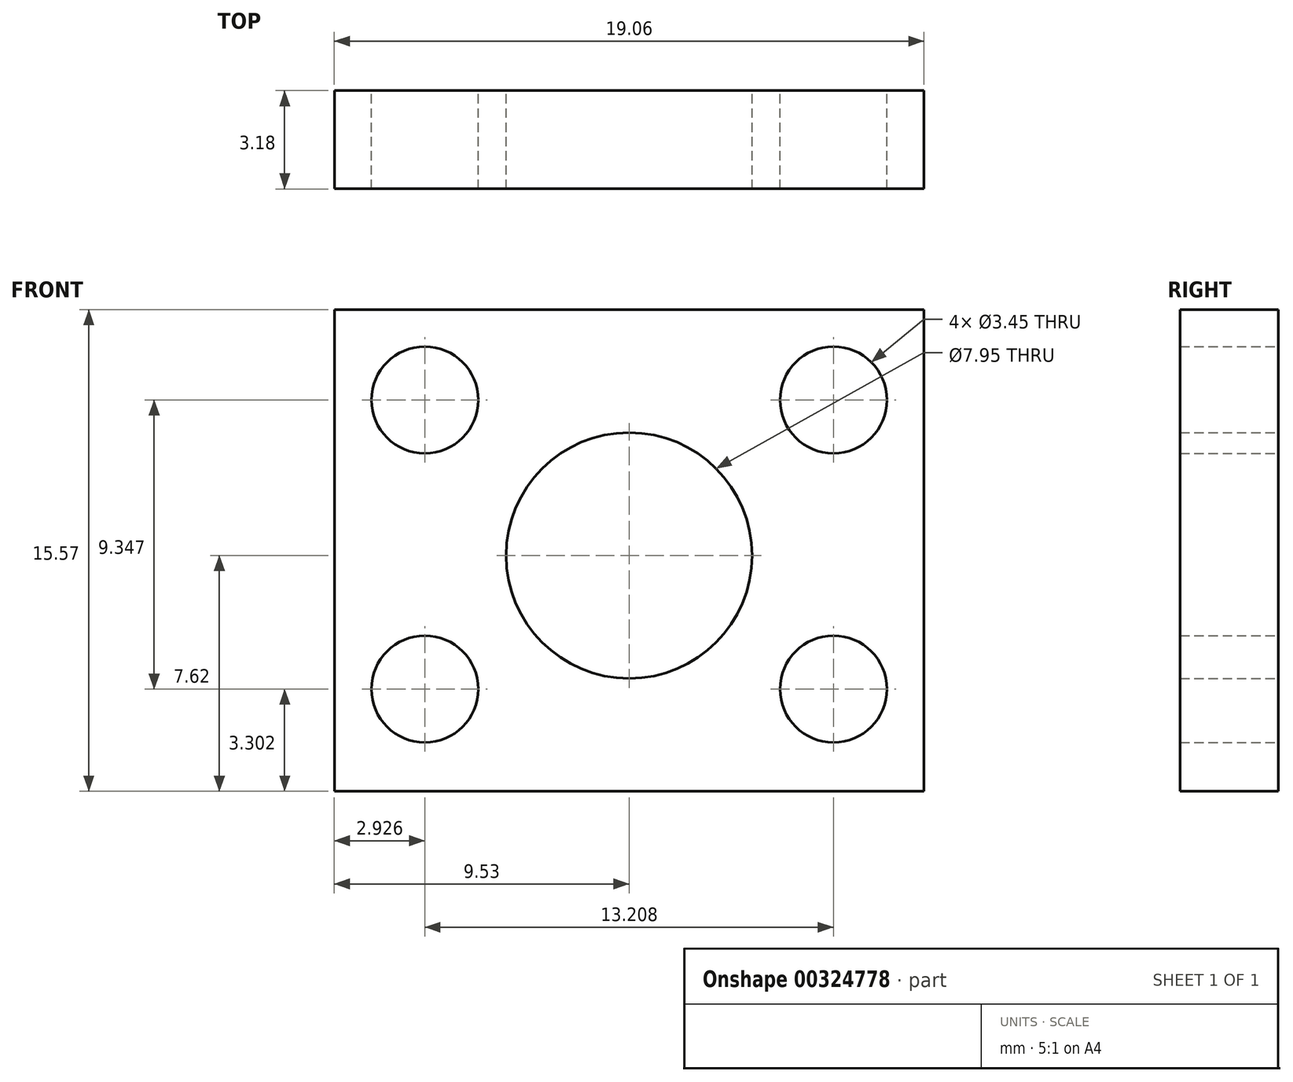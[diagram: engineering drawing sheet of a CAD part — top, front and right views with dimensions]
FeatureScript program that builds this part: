
annotation { "Feature Type Name" : "Feature", "Feature Type Description" : "" }
export const myFeature = defineFeature(function(context is Context, id is Id, definition is map)
    precondition{}
    {
        {
            var Q0;
            Q0=qCreatedBy(makeId("Front.planeOp"),FACE);
            var sketch = newSketch(context, id + "F0", { "sketchPlane" : qUnion([Q0])});
            skLineSegment(sketch, "E0", {"start": v(-9.53, 7.95) * mm, "end": v(9.53, 7.95) * mm});
            skLineSegment(sketch, "E1", {"start": v(-9.53, -7.62) * mm, "end": v(9.53, -7.62) * mm});
            skLineSegment(sketch, "E2", {"start": v(-9.53, 7.95) * mm, "end": v(-9.53, -7.62) * mm});
            skLineSegment(sketch, "E3", {"start": v(9.53, 7.95) * mm, "end": v(9.53, -7.62) * mm});
            skCircle(sketch, "E4", {"center": v(0, 0) * mm, "radius": 3.98 * mm});
            skSolve(sketch);
        }
        {
            var Q0;
            Q0=makeQuery(id+"F0.imprint","IMPRINT",FACE,{"disambiguationData":[TD([[makeQuery(id+"F0.imprint","IMPRINT",EDGE,{"derivedFrom":sQuery(id+"F0.wireOp",EDGE,"E0")}),-1.0]])]});
            extrude(context, id + "F1", {"entities" : qUnion([Q0]), "depth" : 3.17 * mm, "offsetDistance" : 25.4 * mm});
        }
        {
            var Q0;
            Q0=makeQuery(id+"F1.opExtrude","CAP_FACE",FACE,{"disambiguationData":[OSD([sQuery(id+"F0.wireOp",EDGE,"E0"),sQuery(id+"F0.wireOp",EDGE,"E1"),sQuery(id+"F0.wireOp",EDGE,"E2"),sQuery(id+"F0.wireOp",EDGE,"E3"),sQuery(id+"F0.wireOp",EDGE,"E4")])],"isStart":false});
            var sketch = newSketch(context, id + "F2", { "sketchPlane" : qUnion([Q0])});
            skPoint(sketch, "E5", {"position": v(-6.6, 5.03) * mm});
            skPoint(sketch, "E6", {"position": v(6.6, 5.03) * mm});
            skPoint(sketch, "E7", {"position": v(6.6, -4.32) * mm});
            skPoint(sketch, "E8", {"position": v(-6.6, -4.32) * mm});
            skSolve(sketch);
        }
        {
            var Q0;
            Q0=sQuery(id+"F2.wireOp",VERTEX,"E5");
            var Q1;
            Q1=sQuery(id+"F2.wireOp",VERTEX,"E6");
            var Q2;
            Q2=sQuery(id+"F2.wireOp",VERTEX,"E7");
            var Q3;
            Q3=sQuery(id+"F2.wireOp",VERTEX,"E8");
            var Q4;
            Q4=makeQuery(id+"F1.opExtrude","SWEPT_BODY",BODY,{"disambiguationData":[OSD([sQuery(id+"F0.wireOp",EDGE,"E0"),sQuery(id+"F0.wireOp",EDGE,"E1"),sQuery(id+"F0.wireOp",EDGE,"E2"),sQuery(id+"F0.wireOp",EDGE,"E3"),sQuery(id+"F0.wireOp",EDGE,"E4")])]});
            hole(context, id + "F3", {"style" : HoleStyle.SIMPLE, "endStyle" : HoleEndStyle.THROUGH, "holeDiameter" : 3.45 * mm, "majorDiameter" : 6.35 * mm, "tappedDepth" : 12.7 * mm, "tapClearance" : 3, "locations" : qUnion([Q0, Q1, Q2, Q3]), "scope" : qUnion([Q4])});
        }
    });
